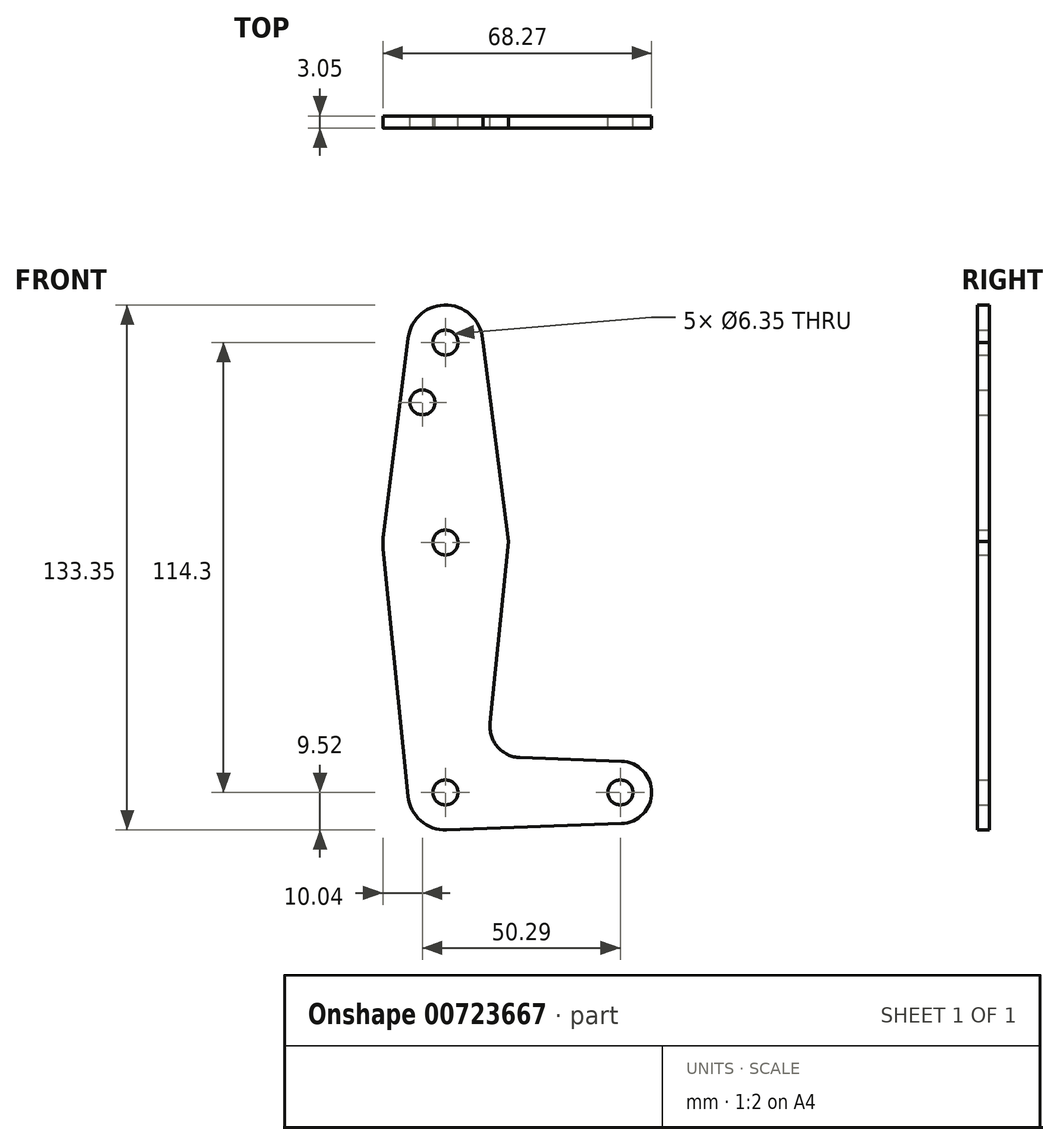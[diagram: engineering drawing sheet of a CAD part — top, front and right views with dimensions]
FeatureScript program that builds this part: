
annotation { "Feature Type Name" : "Feature", "Feature Type Description" : "" }
export const myFeature = defineFeature(function(context is Context, id is Id, definition is map)
    precondition{}
    {
        {
            var Q0;
            Q0=qCreatedBy(makeId("Front.planeOp"),FACE);
            var sketch = newSketch(context, id + "F0", { "sketchPlane" : qUnion([Q0])});
            skLineSegment(sketch, "E0", {"start": v(0, 114.3) * mm, "end": v(0, 0) * mm, "construction": true});
            skCircle(sketch, "E1", {"center": v(0, 114.3) * mm, "radius": 9.53 * mm});
            skCircle(sketch, "E2", {"center": v(0, 0) * mm, "radius": 9.53 * mm});
            skCircle(sketch, "E3", {"center": v(0, 63.5) * mm, "radius": 15.88 * mm});
            skLineSegment(sketch, "E4", {"start": v(9.52, 114.3) * mm, "end": v(15.98, 63.71) * mm});
            skLineSegment(sketch, "E5", {"start": v(15.98, 63.71) * mm, "end": v(11.34, 17.6) * mm});
            skLineSegment(sketch, "E6", {"start": v(-9.45, 115.5) * mm, "end": v(-15.75, 65.48) * mm});
            skLineSegment(sketch, "E7", {"start": v(-15.8, 61.91) * mm, "end": v(-9.48, -0.95) * mm});
            skCircle(sketch, "E8", {"center": v(0, 114.3) * mm, "radius": 3.18 * mm});
            skCircle(sketch, "E9", {"center": v(-5.84, 99.1) * mm, "radius": 3.18 * mm});
            skCircle(sketch, "E10", {"center": v(0, 63.5) * mm, "radius": 3.18 * mm});
            skCircle(sketch, "E11", {"center": v(0, 0) * mm, "radius": 3.18 * mm});
            skLineSegment(sketch, "E12", {"start": v(0, 0) * mm, "end": v(44.45, 0) * mm, "construction": true});
            skCircle(sketch, "E13", {"center": v(44.45, 0) * mm, "radius": 7.94 * mm});
            skLineSegment(sketch, "E14", {"start": v(0.34, -9.52) * mm, "end": v(44.73, -7.93) * mm});
            skLineSegment(sketch, "E15", {"start": v(18.97, 8.85) * mm, "end": v(44.73, 7.93) * mm});
            skArc(sketch, "E16.filletArc", {"start": v(11.34, 17.6) * mm, "mid": v(13.26, 11.57) * mm, "end": v(18.97, 8.85) * mm});
            skCircle(sketch, "E17", {"center": v(44.45, 0) * mm, "radius": 3.18 * mm});
            skSolve(sketch);
        }
        {
            var Q0;
            Q0 = qSketchRegion(id + "F0", true);
            extrude(context, id + "F1", {"entities" : qUnion([Q0]), "depth" : 3.05 * mm, "offsetDistance" : 25.4 * mm});
        }
    });
